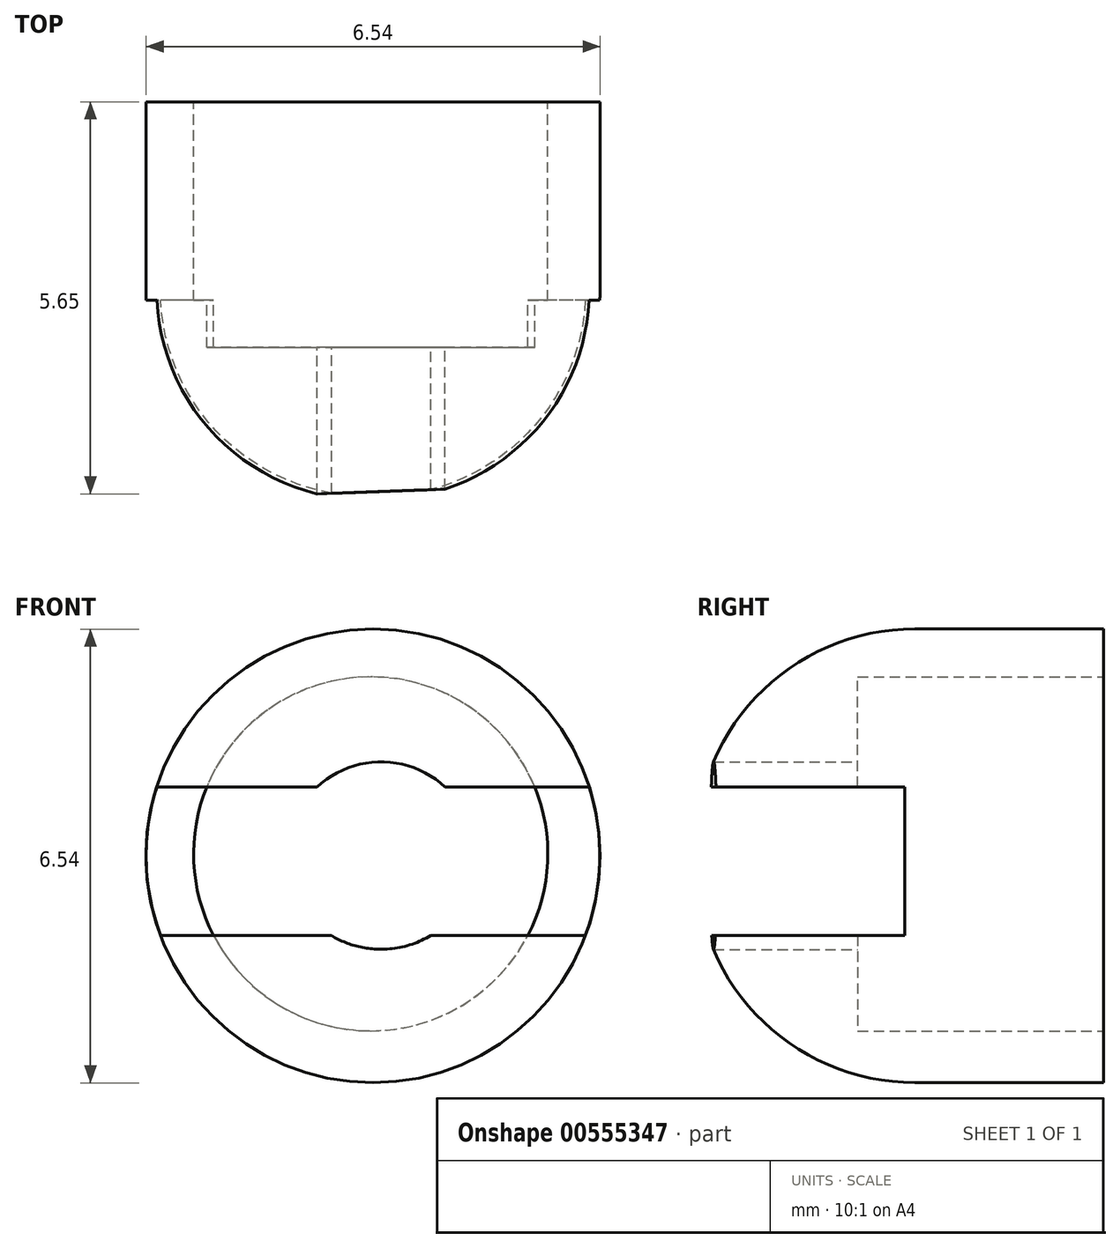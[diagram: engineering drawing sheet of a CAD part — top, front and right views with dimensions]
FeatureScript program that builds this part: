
annotation { "Feature Type Name" : "Feature", "Feature Type Description" : "" }
export const myFeature = defineFeature(function(context is Context, id is Id, definition is map)
    precondition{}
    {
        {
            var Q0;
            Q0=qCreatedBy(makeId("Front.planeOp"),FACE);
            var sketch = newSketch(context, id + "F0", { "sketchPlane" : qUnion([Q0])});
            skCircle(sketch, "E0", {"center": v(-25.37, 25.1) * mm, "radius": 3.27 * mm});
            skSolve(sketch);
        }
        {
            var Q0;
            Q0=makeQuery(id+"F0.imprint","IMPRINT",FACE,{"disambiguationData":[TD([[makeQuery(id+"F0.imprint","IMPRINT",EDGE,{"derivedFrom":sQuery(id+"F0.wireOp",EDGE,"E0")}),1.0]])]});
            extrude(context, id + "F1", {"entities" : qUnion([Q0]), "depth" : 5.87 * mm, "offsetDistance" : 25.4 * mm});
        }
        {
            var Q0;
            Q0=makeQuery(id+"F1.opExtrude","CAP_FACE",FACE,{"disambiguationData":[OSD([sQuery(id+"F0.wireOp",EDGE,"E0")])],"isStart":false});
            fillet(context, id + "F2", {"entities" : qUnion([Q0]), "radius" : 3.15 * mm, "tangentPropagation" : true, "allowEdgeOverflow" : false});
        }
        {
            var Q0;
            Q0=makeQuery(id+"F1.opExtrude","CAP_FACE",FACE,{"disambiguationData":[OSD([sQuery(id+"F0.wireOp",EDGE,"E0")])],"isStart":false});
            var sketch = newSketch(context, id + "F3", { "sketchPlane" : qUnion([Q0])});
            skLineSegment(sketch, "E1.bottom", {"start": v(-19.1, 23.96) * mm, "end": v(-31.95, 23.96) * mm});
            skLineSegment(sketch, "E1.top", {"start": v(-19.1, 26.1) * mm, "end": v(-31.95, 26.1) * mm});
            skLineSegment(sketch, "E1.left", {"start": v(-19.1, 23.96) * mm, "end": v(-19.1, 26.1) * mm});
            skLineSegment(sketch, "E1.right", {"start": v(-31.95, 23.96) * mm, "end": v(-31.95, 26.1) * mm});
            skSolve(sketch);
        }
        {
            var Q0;
            Q0 = qSketchRegion(id + "F3", true);
            extrude(context, id + "F4", {"entities" : qUnion([Q0]), "operationType" : NewBodyOperationType.REMOVE, "oppositeDirection" : true, "depth" : 3 * mm, "offsetDistance" : 25.4 * mm});
        }
        {
            var Q0;
            Q0=qCreatedBy(makeId("Front.planeOp"),FACE);
            var sketch = newSketch(context, id + "F5", { "sketchPlane" : qUnion([Q0])});
            skCircle(sketch, "E2", {"center": v(-25.26, 25.1) * mm, "radius": 1.35 * mm});
            skSolve(sketch);
        }
        {
            var Q0;
            Q0 = qSketchRegion(id + "F5", true);
            extrude(context, id + "F6", {"entities" : qUnion([Q0]), "operationType" : NewBodyOperationType.REMOVE, "depth" : 25.4 * mm, "offsetDistance" : 25.4 * mm});
        }
        {
            var Q0;
            Q0=qCreatedBy(makeId("Front.planeOp"),FACE);
            var sketch = newSketch(context, id + "F7", { "sketchPlane" : qUnion([Q0])});
            skCircle(sketch, "E3", {"center": v(-25.4, 25.13) * mm, "radius": 2.55 * mm});
            skSolve(sketch);
        }
        {
            var Q0;
            Q0=makeQuery(id+"F7.imprint","IMPRINT",FACE,{"disambiguationData":[TD([[makeQuery(id+"F7.imprint","IMPRINT",EDGE,{"derivedFrom":sQuery(id+"F7.wireOp",EDGE,"E3")}),1.0]])]});
            extrude(context, id + "F8", {"entities" : qUnion([Q0]), "operationType" : NewBodyOperationType.REMOVE, "depth" : 3.54 * mm, "offsetDistance" : 25.4 * mm});
        }
    });
